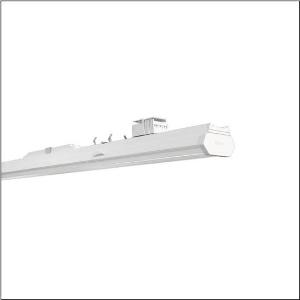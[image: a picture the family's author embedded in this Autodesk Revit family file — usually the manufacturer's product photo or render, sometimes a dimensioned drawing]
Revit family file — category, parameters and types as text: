
# Revit family: licross_r__21_protected_ho_52td12dn4e5m3s4_bb7a
name_source: partatom
category: Lighting Fixtures
units: mm (PartAtom-declared; Revit-internal decimal feet)

## family parameters
Cut with Voids When Loaded = No
Host = Face
Light Source = No
Part Type = Normal
Room Calculation Point = No
Round Connector Dimension = Use Diameter
Shared = No

## types (1)
- --- (1 x LED, 910 lm, 7.6 W, 4000K)
    Apparent Load = 8 VA
    CIE Flux Codes = 70 91 97 98 100
    Color Rendering = 80
    Color Temperature = 4000K
    Default Elevation = 1800 mm
    Description = Licross® 21 Protected HO, luminaire insert, of sheet steel, galvanised, coil coated, white, length: 1.500mm, width: 90mm, height: 103mm, LED rated luminous flux: 14.690lm, light colour: 840, control gear: DALI 2, with plug, 6-pole, with phase selection, for trunking rail, 9 or 11-core, mains connection: 220..240V, AC, 50/60Hz, rated input power: 89W, for trunking rail, 9-/11-core, halogen-free wiring, for emergency light function, converter,control gear: single battery element, battery: LiFeP04, 9Ah, primary light control with lens, of plastic, primary optical cover: cover, of PMMA, light emission: direct distribution, primary light characteristic: symmetric, protection rating (complete): IP54, insulation class (complete): insulation class I (protective earthing), certification: CE, UKCA, protection symbol: D if used in an environment with non-conductive dust loads with corresponding accessories, impact resistance: IK06, permissible ambient temperature for indoor applications: +5..+30°C, standard: EN 60598-2-22, LABS conformity tested according to VDMA 24364:2018-05, reducing of maximum allowable ambient temperature of 5°C with ceiling mounting, corresponds to IFS (International Featured Standards) requirements for safety and quality in the food industry, packaging unit: 1 piece
    Height = 92 mm
    Lamp = 1 x LED
    Lamp Light Flux = 910 lm
    Lamp Power = 7.6 W
    Lamp count = 1
    Length = 1500 mm
    Luminous efficacy = 120 lm/W
    Manufacturer = Siteco
    ModVariant = No
    Model = 52TD12DN4E5M3S4
    Mounting Place = Ceiling
    Mounting Type = Pendant
    Number of Poles = 1
    OnlyDefault = Yes
    Power Factor = 1
    Product Name = Licross® 21 Protected HO
    Product group = luminaire insert
    ProductGroupID = 901
    Protection Class = Protection class I
    Protection Degree = IP 54
    RLX_Detail_Level = 1
    RLX_Emergency_Light_Flux = 0 lm
    RLX_Emergency_Type = 0
    RLX_Emergency_Type_DB = No
    RlxData = <blob elided: 24953 chars, md5=69bb7f39>
    Socket = socket
    Standby Power = 0 W
    System Light Flux = 910 lm
    System Power = 8 W
    Type Comments = : emergency light operation: 3 h
    Type Image = l_1256148.jpg
    URL = http://relux.com
    VarID = @adj_059465
    Voltage = 0 V
    Weight = 0.00 kg
    Width = 88 mm

## geometry (parser evidence)
native form markers: Blend x4, Sweep x11
no freeform markers — native parametric forms only
